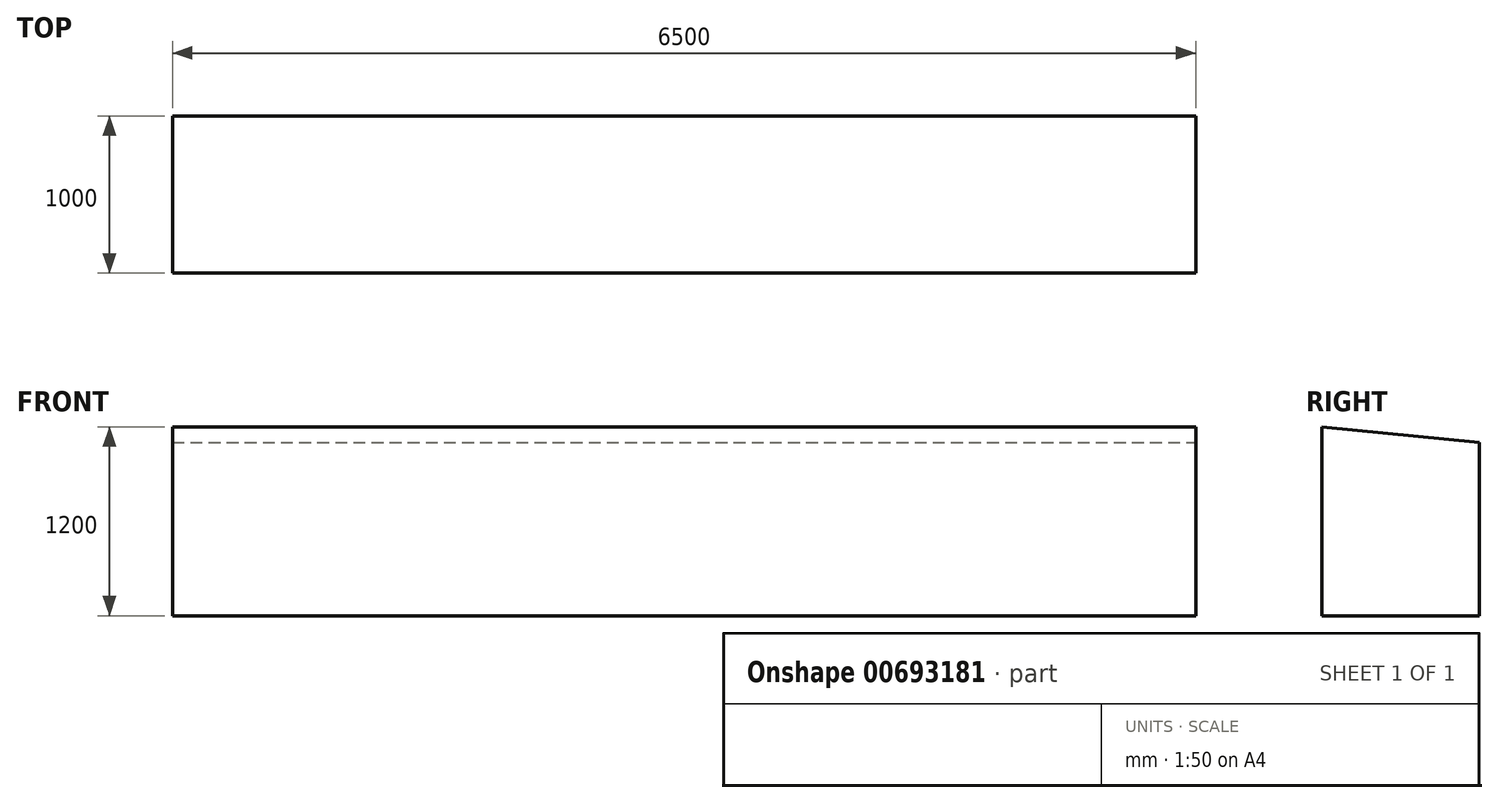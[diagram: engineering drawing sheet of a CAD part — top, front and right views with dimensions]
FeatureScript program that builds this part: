
annotation { "Feature Type Name" : "Feature", "Feature Type Description" : "" }
export const myFeature = defineFeature(function(context is Context, id is Id, definition is map)
    precondition{}
    {
        {
            var Q0;
            Q0=qCreatedBy(makeId("Top.planeOp"),FACE);
            var sketch = newSketch(context, id + "F0", { "sketchPlane" : qUnion([Q0])});
            skLineSegment(sketch, "E0.bottom", {"start": v(-3245.04, -770.94) * mm, "end": v(3254.96, -770.94) * mm});
            skLineSegment(sketch, "E0.top", {"start": v(-3245.04, -1770.94) * mm, "end": v(3254.96, -1770.94) * mm});
            skLineSegment(sketch, "E0.left", {"start": v(-3245.04, -770.94) * mm, "end": v(-3245.04, -1770.94) * mm});
            skLineSegment(sketch, "E0.right", {"start": v(3254.96, -770.94) * mm, "end": v(3254.96, -1770.94) * mm});
            skSolve(sketch);
        }
        {
            var Q0;
            Q0=makeQuery(id+"F0.imprint","IMPRINT",FACE,{"disambiguationData":[TD([[makeQuery(id+"F0.imprint","IMPRINT",EDGE,{"derivedFrom":sQuery(id+"F0.wireOp",EDGE,"E0.bottom")}),-1.0]])]});
            extrude(context, id + "F1", {"entities" : qUnion([Q0]), "depth" : 1200 * mm, "offsetDistance" : 25.4 * mm});
        }
        {
            var Q0;
            Q0=makeQuery(id+"F1.opExtrude","SWEPT_FACE",FACE,{"disambiguationData":[OSD([sQuery(id+"F0.wireOp",EDGE,"E0.right")])]});
            var sketch = newSketch(context, id + "F2", { "sketchPlane" : qUnion([Q0])});
            skLineSegment(sketch, "E1", {"start": v(-1770.94, 1200) * mm, "end": v(-770.94, 1100) * mm});
            skLineSegment(sketch, "E2", {"start": v(-770.94, 1100) * mm, "end": v(-770.94, 1200) * mm});
            skLineSegment(sketch, "E3", {"start": v(-770.94, 1200) * mm, "end": v(-1770.94, 1200) * mm});
            skSolve(sketch);
        }
        {
            var Q0;
            Q0=makeQuery(id+"F2.imprint","IMPRINT",FACE,{"disambiguationData":[TD([[makeQuery(id+"F2.imprint","IMPRINT",EDGE,{"derivedFrom":sQuery(id+"F2.wireOp",EDGE,"E1")}),1.0]])]});
            extrude(context, id + "F3", {"entities" : qUnion([Q0]), "operationType" : NewBodyOperationType.REMOVE, "endBound" : BoundingType.UP_TO_NEXT, "oppositeDirection" : true, "depth" : 25.4 * mm, "offsetDistance" : 25.4 * mm});
        }
    });
